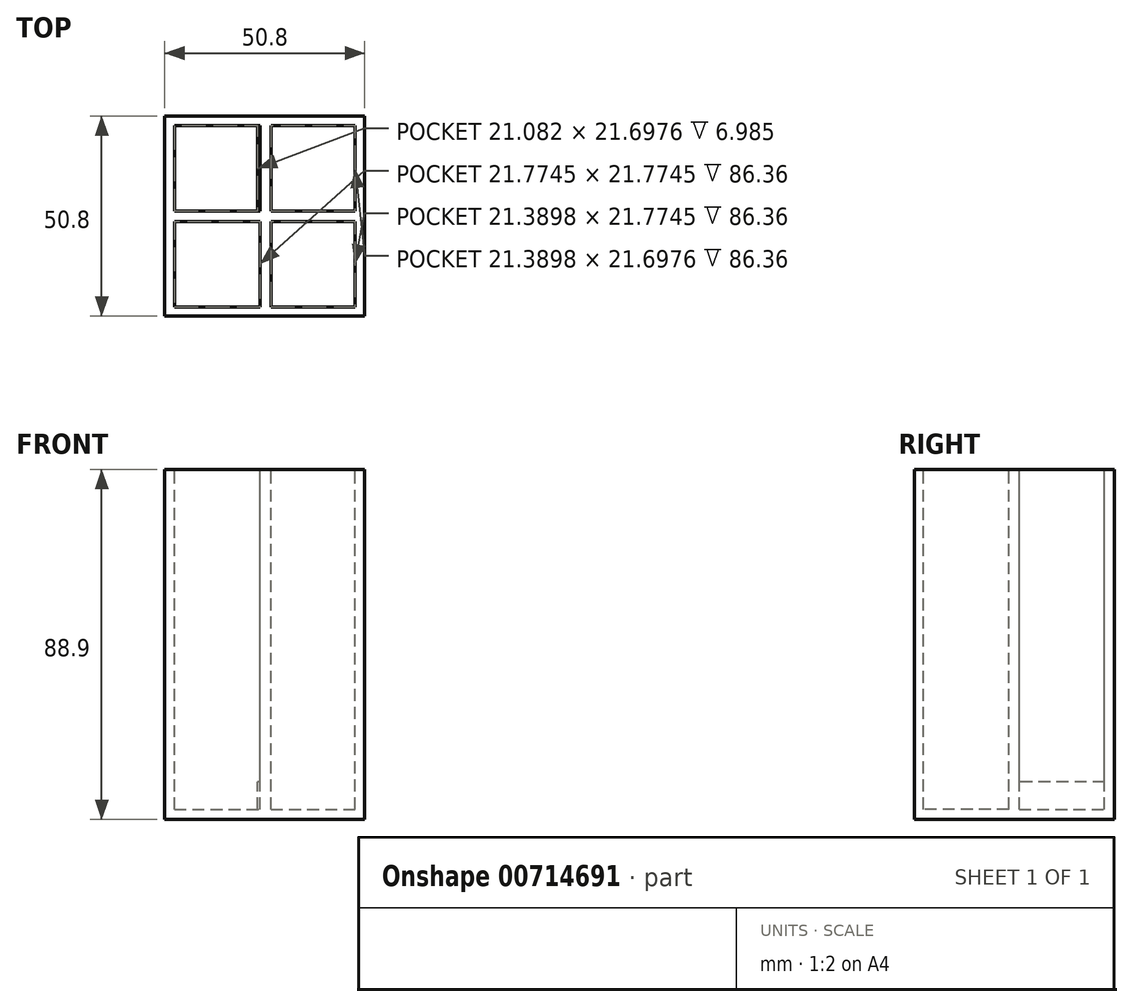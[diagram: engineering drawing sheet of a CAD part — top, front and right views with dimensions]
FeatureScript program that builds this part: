
annotation { "Feature Type Name" : "Feature", "Feature Type Description" : "" }
export const myFeature = defineFeature(function(context is Context, id is Id, definition is map)
    precondition{}
    {
        {
            var Q0;
            Q0=qCreatedBy(makeId("Top.planeOp"),FACE);
            var sketch = newSketch(context, id + "F0", { "sketchPlane" : qUnion([Q0])});
            skLineSegment(sketch, "E0.bottom", {"start": v(25.4, -25.4) * mm, "end": v(-25.4, -25.4) * mm});
            skLineSegment(sketch, "E0.top", {"start": v(25.4, 25.4) * mm, "end": v(-25.4, 25.4) * mm});
            skLineSegment(sketch, "E0.left", {"start": v(25.4, -25.4) * mm, "end": v(25.4, 25.4) * mm});
            skLineSegment(sketch, "E0.right", {"start": v(-25.4, -25.4) * mm, "end": v(-25.4, 25.4) * mm});
            skPoint(sketch, "E0.middle", {"position": v(0, 0) * mm});
            skSolve(sketch);
        }
        {
            var Q0;
            Q0 = qSketchRegion(id + "F0", true);
            extrude(context, id + "F1", {"entities" : qUnion([Q0]), "depth" : 88.9 * mm, "offsetDistance" : 25.4 * mm});
        }
        {
            var Q0;
            Q0=makeQuery(id+"F1.opExtrude","CAP_FACE",FACE,{"disambiguationData":[OSD([sQuery(id+"F0.wireOp",EDGE,"E0.bottom"),sQuery(id+"F0.wireOp",EDGE,"E0.top"),sQuery(id+"F0.wireOp",EDGE,"E0.left"),sQuery(id+"F0.wireOp",EDGE,"E0.right")])],"isStart":false});
            var sketch = newSketch(context, id + "F2", { "sketchPlane" : qUnion([Q0])});
            skLineSegment(sketch, "E1.bottom", {"start": v(-22.97, 22.97) * mm, "end": v(-1.89, 22.97) * mm});
            skLineSegment(sketch, "E1.top", {"start": v(-22.97, 1.27) * mm, "end": v(-1.89, 1.27) * mm});
            skLineSegment(sketch, "E1.left", {"start": v(-22.97, 22.97) * mm, "end": v(-22.97, 1.27) * mm});
            skLineSegment(sketch, "E1.right", {"start": v(-1.89, 22.97) * mm, "end": v(-1.89, 1.27) * mm});
            skLineSegment(sketch, "E2.bottom", {"start": v(-22.97, -1.35) * mm, "end": v(-1.2, -1.35) * mm});
            skLineSegment(sketch, "E2.top", {"start": v(-22.97, -23.12) * mm, "end": v(-1.2, -23.12) * mm});
            skLineSegment(sketch, "E2.left", {"start": v(-22.97, -1.35) * mm, "end": v(-22.97, -23.12) * mm});
            skLineSegment(sketch, "E2.right", {"start": v(-1.2, -1.35) * mm, "end": v(-1.2, -23.12) * mm});
            skLineSegment(sketch, "E3.bottom", {"start": v(1.58, -1.35) * mm, "end": v(22.97, -1.35) * mm});
            skLineSegment(sketch, "E3.top", {"start": v(1.58, -23.12) * mm, "end": v(22.97, -23.12) * mm});
            skLineSegment(sketch, "E3.left", {"start": v(1.58, -1.35) * mm, "end": v(1.58, -23.12) * mm});
            skLineSegment(sketch, "E3.right", {"start": v(22.97, -1.35) * mm, "end": v(22.97, -23.12) * mm});
            skLineSegment(sketch, "E4.bottom", {"start": v(1.58, 1.27) * mm, "end": v(22.97, 1.27) * mm});
            skLineSegment(sketch, "E4.top", {"start": v(1.58, 22.97) * mm, "end": v(22.97, 22.97) * mm});
            skLineSegment(sketch, "E4.left", {"start": v(1.58, 1.27) * mm, "end": v(1.58, 22.97) * mm});
            skLineSegment(sketch, "E4.right", {"start": v(22.97, 1.27) * mm, "end": v(22.97, 22.97) * mm});
            skSolve(sketch);
        }
        {
            var Q0;
            Q0=makeQuery(id+"F2.imprint","IMPRINT",FACE,{"disambiguationData":[TD([[makeQuery(id+"F2.imprint","IMPRINT",EDGE,{"derivedFrom":sQuery(id+"F2.wireOp",EDGE,"E2.bottom")}),-1.0]])]});
            var Q1;
            Q1=makeQuery(id+"F2.imprint","IMPRINT",FACE,{"disambiguationData":[TD([[makeQuery(id+"F2.imprint","IMPRINT",EDGE,{"derivedFrom":sQuery(id+"F2.wireOp",EDGE,"E3.bottom")}),-1.0]])]});
            var Q2;
            Q2=makeQuery(id+"F2.imprint","IMPRINT",FACE,{"disambiguationData":[TD([[makeQuery(id+"F2.imprint","IMPRINT",EDGE,{"derivedFrom":sQuery(id+"F2.wireOp",EDGE,"E4.bottom")}),1.0]])]});
            extrude(context, id + "F3", {"entities" : qUnion([Q0, Q1, Q2]), "operationType" : NewBodyOperationType.REMOVE, "oppositeDirection" : true, "depth" : 79.38 * mm, "offsetDistance" : 25.4 * mm});
        }
        {
            var Q0;
            Q0 = qSketchRegion(id + "F2", true);
            extrude(context, id + "F4", {"entities" : qUnion([Q0]), "operationType" : NewBodyOperationType.REMOVE, "oppositeDirection" : true, "depth" : 86.36 * mm, "offsetDistance" : 25.4 * mm});
        }
        {
            var Q0;
            Q0=makeQuery(id+"F1.opExtrude","CAP_FACE",FACE,{"disambiguationData":[OSD([sQuery(id+"F0.wireOp",EDGE,"E0.bottom"),sQuery(id+"F0.wireOp",EDGE,"E0.top"),sQuery(id+"F0.wireOp",EDGE,"E0.left"),sQuery(id+"F0.wireOp",EDGE,"E0.right")])],"isStart":false});
            var sketch = newSketch(context, id + "F5", { "sketchPlane" : qUnion([Q0])});
            skLineSegment(sketch, "E5.bottom", {"start": v(-1.2, 1.27) * mm, "end": v(-1.89, 1.27) * mm});
            skLineSegment(sketch, "E5.top", {"start": v(-1.2, 22.97) * mm, "end": v(-1.89, 22.97) * mm});
            skLineSegment(sketch, "E5.left", {"start": v(-1.2, 1.27) * mm, "end": v(-1.2, 22.97) * mm});
            skLineSegment(sketch, "E5.right", {"start": v(-1.89, 1.27) * mm, "end": v(-1.89, 22.97) * mm});
            skSolve(sketch);
        }
        {
            var Q0;
            Q0 = qSketchRegion(id + "F5", true);
            extrude(context, id + "F6", {"entities" : qUnion([Q0]), "operationType" : NewBodyOperationType.REMOVE, "oppositeDirection" : true, "depth" : 79.38 * mm, "offsetDistance" : 25.4 * mm});
        }
    });
